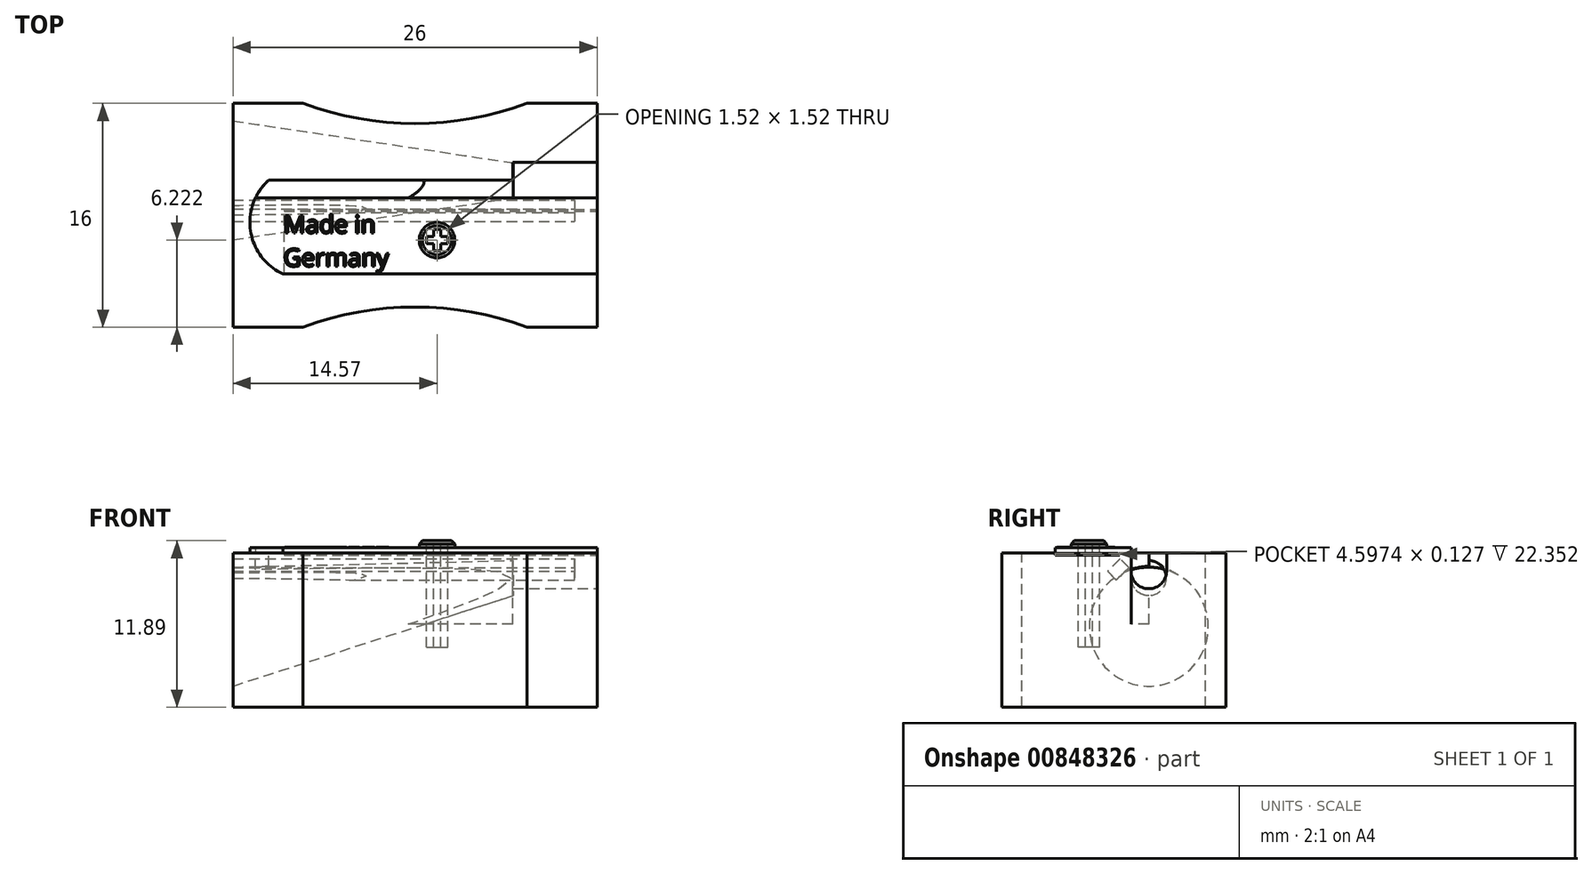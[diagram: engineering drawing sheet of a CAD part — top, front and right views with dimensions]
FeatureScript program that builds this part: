
annotation { "Feature Type Name" : "Feature", "Feature Type Description" : "" }
export const myFeature = defineFeature(function(context is Context, id is Id, definition is map)
    precondition{}
    {
        {
            var Q0;
            Q0=qCreatedBy(makeId("Top.planeOp"),FACE);
            var sketch = newSketch(context, id + "F0", { "sketchPlane" : qUnion([Q0])});
            skLineSegment(sketch, "E0.bottom", {"start": v(-13, 8) * mm, "end": v(13, 8) * mm});
            skLineSegment(sketch, "E0.top", {"start": v(-13, -8) * mm, "end": v(13, -8) * mm});
            skLineSegment(sketch, "E0.left", {"start": v(-13, 8) * mm, "end": v(-13, -8) * mm});
            skLineSegment(sketch, "E0.right", {"start": v(13, 8) * mm, "end": v(13, -8) * mm});
            skSolve(sketch);
        }
        {
            var Q0;
            Q0=makeQuery(id+"F0.imprint","IMPRINT",FACE,{"disambiguationData":[TD([[makeQuery(id+"F0.imprint","IMPRINT",EDGE,{"derivedFrom":sQuery(id+"F0.wireOp",EDGE,"E0.bottom")}),-1.0]])]});
            extrude(context, id + "F1", {"entities" : qUnion([Q0]), "depth" : 11 * mm, "offsetDistance" : 25.4 * mm});
        }
        {
            var Q0;
            Q0=makeQuery(id+"F1.opExtrude","CAP_FACE",FACE,{"disambiguationData":[OSD([sQuery(id+"F0.wireOp",EDGE,"E0.bottom"),sQuery(id+"F0.wireOp",EDGE,"E0.top"),sQuery(id+"F0.wireOp",EDGE,"E0.left"),sQuery(id+"F0.wireOp",EDGE,"E0.right")])],"isStart":false});
            var sketch = newSketch(context, id + "F2", { "sketchPlane" : qUnion([Q0])});
            skArc(sketch, "E1", {"start": v(8, -8) * mm, "mid": v(0, -6.55) * mm, "end": v(-8, -8) * mm});
            skArc(sketch, "E2", {"start": v(-8, 8) * mm, "mid": v(0, 6.55) * mm, "end": v(8, 8) * mm});
            skSolve(sketch);
        }
        {
            var Q0;
            {var subQ0=sQuery(id+"F2.wireOp",EDGE,"E2");Q0=makeQuery(id+"F2.imprint","IMPRINT",FACE,{"disambiguationData":[TD([[makeQuery(id+"F2.imprint","IMPRINT",EDGE,{"derivedFrom":subQ0}),1.0]])]});}
            var Q1;
            {var subQ0=sQuery(id+"F2.wireOp",EDGE,"E1");Q1=makeQuery(id+"F2.imprint","IMPRINT",FACE,{"disambiguationData":[TD([[makeQuery(id+"F2.imprint","IMPRINT",EDGE,{"derivedFrom":subQ0}),1.0]])]});}
            extrude(context, id + "F3", {"entities" : qUnion([Q0, Q1]), "operationType" : NewBodyOperationType.REMOVE, "endBound" : BoundingType.THROUGH_ALL, "oppositeDirection" : true, "depth" : 25.4 * mm, "offsetDistance" : 25.4 * mm});
        }
        {
            var Q0;
            Q0=makeQuery(id+"F1.opExtrude","SWEPT_FACE",FACE,{"disambiguationData":[OSD([sQuery(id+"F0.wireOp",EDGE,"E0.left")])]});
            var sketch = newSketch(context, id + "F4", { "sketchPlane" : qUnion([Q0])});
            skCircle(sketch, "E3", {"center": v(-2.5, 5.75) * mm, "radius": 4.25 * mm});
            skSolve(sketch);
        }
        {
            var Q0;
            Q0=qCreatedBy(makeId("Right.planeOp"),FACE);
            cPlane(context, id + "F5", {"entities" : qUnion([Q0]), "cplaneType" : CPlaneType.OFFSET, "offset" : 7 * mm, "width" : 152.4 * mm, "height" : 152.4 * mm});
        }
        {
            var Q0;
            Q0=qCreatedBy(id+"F5.planeOp",FACE);
            var sketch = newSketch(context, id + "F6", { "sketchPlane" : qUnion([Q0])});
            skCircle(sketch, "E4", {"center": v(2.5, 9.22) * mm, "radius": 1.25 * mm});
            skSolve(sketch);
        }
        {
            var Q0;
            Q0=qCreatedBy(makeId("Front.planeOp"),FACE);
            cPlane(context, id + "F7", {"entities" : qUnion([Q0]), "cplaneType" : CPlaneType.OFFSET, "offset" : 2.5 * mm, "oppositeDirection" : true, "width" : 152.4 * mm, "height" : 152.4 * mm});
        }
        {
            var Q0;
            Q0=qCreatedBy(id+"F7.planeOp",FACE);
            var sketch = newSketch(context, id + "F8", { "sketchPlane" : qUnion([Q0])});
            skLineSegment(sketch, "E5", {"start": v(-13, 5.75) * mm, "end": v(7, 9.22) * mm});
            skSolve(sketch);
        }
        {
            var Q0;
            Q0=sQuery(id+"F8.wireOp",EDGE,"E5");
            var Q1;
            Q1=makeQuery(id+"F4.imprint","IMPRINT",FACE,{"disambiguationData":[TD([[makeQuery(id+"F4.imprint","IMPRINT",EDGE,{"derivedFrom":sQuery(id+"F4.wireOp",EDGE,"E3")}),1.0]])]});
            var Q2;
            Q2 = qSketchRegion(id + "F6", true);
            loft(context, id + "F9", {"operationType" : NewBodyOperationType.REMOVE, "addSections" : true, "spine" : qUnion([Q0]), "sectionCount" : 2, "sheetProfilesArray" : [{ "sheetProfileEntities" : qUnion([Q1]) }, { "sheetProfileEntities" : qUnion([Q2]) }]});
        }
        {
            var Q0;
            Q0=makeQuery(id+"F1.opExtrude","SWEPT_FACE",FACE,{"disambiguationData":[OSD([sQuery(id+"F0.wireOp",EDGE,"E0.right")])]});
            var sketch = newSketch(context, id + "F10", { "sketchPlane" : qUnion([Q0])});
            skArc(sketch, "E6", {"start": v(1.23, 9.73) * mm, "mid": v(2.5, 8.46) * mm, "end": v(3.77, 9.73) * mm});
            skLineSegment(sketch, "E7", {"start": v(1.23, 9.73) * mm, "end": v(1.23, 11) * mm});
            skLineSegment(sketch, "E8", {"start": v(3.77, 9.73) * mm, "end": v(3.77, 11) * mm});
            skSolve(sketch);
        }
        {
            var Q0;
            Q0=makeQuery(id+"F10.imprint","IMPRINT",FACE,{"disambiguationData":[TD([[makeQuery(id+"F10.imprint","IMPRINT",EDGE,{"derivedFrom":sQuery(id+"F10.wireOp",EDGE,"E6")}),1.0]])]});
            extrude(context, id + "F11", {"entities" : qUnion([Q0]), "operationType" : NewBodyOperationType.REMOVE, "oppositeDirection" : true, "depth" : 6.02 * mm, "offsetDistance" : 25.4 * mm});
        }
        {
            var Q0;
            Q0=makeQuery(id+"F1.opExtrude","CAP_FACE",FACE,{"disambiguationData":[OSD([sQuery(id+"F0.wireOp",EDGE,"E0.bottom"),sQuery(id+"F0.wireOp",EDGE,"E0.top"),sQuery(id+"F0.wireOp",EDGE,"E0.left"),sQuery(id+"F0.wireOp",EDGE,"E0.right")])],"isStart":false});
            var sketch = newSketch(context, id + "F12", { "sketchPlane" : qUnion([Q0])});
            skLineSegment(sketch, "E9", {"start": v(6.98, 2.5) * mm, "end": v(-10.46, 2.5) * mm});
            skArc(sketch, "E10", {"start": v(-10.46, 2.5) * mm, "mid": v(-11.74, -1.12) * mm, "end": v(-9.44, -4.2) * mm});
            skLineSegment(sketch, "E11", {"start": v(-9.44, -4.2) * mm, "end": v(13, -4.2) * mm});
            skLineSegment(sketch, "E12", {"start": v(13, 1.23) * mm, "end": v(-11.4, 1.23) * mm});
            skSolve(sketch);
        }
        {
            var Q0;
            {var subQ0=sQuery(id+"F12.wireOp",EDGE,"E9");Q0=makeQuery(id+"F12.imprint","IMPRINT",FACE,{"disambiguationData":[TD([[makeQuery(id+"F12.imprint","IMPRINT",EDGE,{"derivedFrom":subQ0}),1.0]])]});}
            extrude(context, id + "F13", {"entities" : qUnion([Q0]), "operationType" : NewBodyOperationType.REMOVE, "oppositeDirection" : true, "depth" : 5.08 * mm, "offsetDistance" : 25.4 * mm});
        }
        {
            var Q0;
            {var subQ8=sQuery(id+"F12.wireOp",EDGE,"E11");Q0=makeQuery(id+"F12.imprint","IMPRINT",FACE,{"disambiguationData":[TD([[makeQuery(id+"F12.imprint","IMPRINT",EDGE,{"derivedFrom":subQ8}),1.0]])]});}
            extrude(context, id + "F14", {"entities" : qUnion([Q0]), "operationType" : NewBodyOperationType.ADD, "depth" : 0.38 * mm, "offsetDistance" : 25.4 * mm});
        }
        {
            var Q0;
            Q0=makeQuery(id+"F14.opExtrude","CAP_EDGE",EDGE,{"disambiguationData":[OSD([sQuery(id+"F12.wireOp",EDGE,"E12")])],"isStart":false});
            cPlane(context, id + "F15", {"entities" : qUnion([Q0]), "cplaneType" : CPlaneType.LINE_ANGLE, "offset" : 25.4 * mm, "angle" : 45 * degree, "width" : 152.4 * mm, "height" : 152.4 * mm});
        }
        {
            var Q0;
            Q0=qCreatedBy(id+"F15.planeOp",FACE);
            var sketch = newSketch(context, id + "F16", { "sketchPlane" : qUnion([Q0])});
            skLineSegment(sketch, "E13.bottom", {"start": v(-13, 7.81) * mm, "end": v(11.4, 7.81) * mm});
            skLineSegment(sketch, "E13.top", {"start": v(-13, 6.54) * mm, "end": v(11.4, 6.54) * mm});
            skLineSegment(sketch, "E13.left", {"start": v(-13, 7.81) * mm, "end": v(-13, 6.54) * mm});
            skLineSegment(sketch, "E13.right", {"start": v(11.4, 7.81) * mm, "end": v(11.4, 6.54) * mm});
            skPoint(sketch, "E14", {"position": v(-13, 7.18) * mm});
            skPoint(sketch, "E15", {"position": v(11.4, 7.18) * mm});
            skSolve(sketch);
        }
        {
            var Q0;
            Q0=makeQuery(id+"F16.imprint","IMPRINT",FACE,{"disambiguationData":[TD([[makeQuery(id+"F16.imprint","IMPRINT",EDGE,{"derivedFrom":sQuery(id+"F16.wireOp",EDGE,"E13.bottom")}),-1.0]])]});
            extrude(context, id + "F17", {"entities" : qUnion([Q0]), "operationType" : NewBodyOperationType.REMOVE, "oppositeDirection" : true, "depth" : 0.89 * mm, "offsetDistance" : 25.4 * mm});
        }
        {
            var Q0;
            Q0=makeQuery(id+"F14.opExtrude","CAP_FACE",FACE,{"disambiguationData":[OSD([sQuery(id+"F0.wireOp",EDGE,"E0.right"),sQuery(id+"F12.wireOp",EDGE,"E10"),sQuery(id+"F12.wireOp",EDGE,"E11"),sQuery(id+"F12.wireOp",EDGE,"E12")])],"isStart":false});
            var sketch = newSketch(context, id + "F18", { "sketchPlane" : qUnion([Q0])});
            skText(sketch, "E16", { "text": "Made in\nGermany", "fontName": "OpenSans-Regular.ttf"});
            skCircle(sketch, "E17", {"center": v(1.57, -1.78) * mm, "radius": 1.27 * mm});
            const initialGuessF18  = {"E16": [-0.0094, -0.00127, 1, 0, 0.00126]};
            skSetInitialGuess(sketch, initialGuessF18);
            skSolve(sketch);
        }
        {
            var Q0;
            Q0=makeQuery(id+"F18.imprint","IMPRINT",FACE,{"disambiguationData":[TD([[makeQuery(id+"F18.imprint","IMPRINT",EDGE,{"derivedFrom":sQuery(id+"F18.wireOp",EDGE,"E16.sketch_text.stroke-0")}),-1.0]])]});
            var Q1;
            Q1=makeQuery(id+"F18.imprint","IMPRINT",FACE,{"disambiguationData":[TD([[makeQuery(id+"F18.imprint","IMPRINT",EDGE,{"derivedFrom":sQuery(id+"F18.wireOp",EDGE,"E16.sketch_text.stroke-88")}),-1.0]])]});
            var Q2;
            Q2=makeQuery(id+"F18.imprint","IMPRINT",FACE,{"disambiguationData":[TD([[makeQuery(id+"F18.imprint","IMPRINT",EDGE,{"derivedFrom":sQuery(id+"F18.wireOp",EDGE,"E16.sketch_text.stroke-92")}),-1.0]])]});
            var Q3;
            Q3=makeQuery(id+"F18.imprint","IMPRINT",FACE,{"disambiguationData":[TD([[makeQuery(id+"F18.imprint","IMPRINT",EDGE,{"derivedFrom":sQuery(id+"F18.wireOp",EDGE,"E16.sketch_text.stroke-100")}),-1.0]])]});
            var Q4;
            Q4=makeQuery(id+"F18.imprint","IMPRINT",FACE,{"disambiguationData":[TD([[makeQuery(id+"F18.imprint","IMPRINT",EDGE,{"derivedFrom":sQuery(id+"F18.wireOp",EDGE,"E16.sketch_text.stroke-117")}),-1.0]])]});
            var Q5;
            Q5=makeQuery(id+"F18.imprint","IMPRINT",FACE,{"disambiguationData":[TD([[makeQuery(id+"F18.imprint","IMPRINT",EDGE,{"derivedFrom":sQuery(id+"F18.wireOp",EDGE,"E16.sketch_text.stroke-156")}),-1.0]])]});
            var Q6;
            Q6=makeQuery(id+"F18.imprint","IMPRINT",FACE,{"disambiguationData":[TD([[makeQuery(id+"F18.imprint","IMPRINT",EDGE,{"derivedFrom":sQuery(id+"F18.wireOp",EDGE,"E16.sketch_text.stroke-169")}),-1.0]])]});
            var Q7;
            Q7=makeQuery(id+"F18.imprint","IMPRINT",FACE,{"disambiguationData":[TD([[makeQuery(id+"F18.imprint","IMPRINT",EDGE,{"derivedFrom":sQuery(id+"F18.wireOp",EDGE,"E16.sketch_text.stroke-224")}),-1.0]])]});
            var Q8;
            Q8=makeQuery(id+"F18.imprint","IMPRINT",FACE,{"disambiguationData":[TD([[makeQuery(id+"F18.imprint","IMPRINT",EDGE,{"derivedFrom":sQuery(id+"F18.wireOp",EDGE,"E16.sketch_text.stroke-241")}),-1.0]])]});
            var Q9;
            Q9=makeQuery(id+"F18.imprint","IMPRINT",FACE,{"disambiguationData":[TD([[makeQuery(id+"F18.imprint","IMPRINT",EDGE,{"derivedFrom":sQuery(id+"F18.wireOp",EDGE,"E16.sketch_text.stroke-18")}),-1.0]])]});
            var Q10;
            Q10=makeQuery(id+"F18.imprint","IMPRINT",FACE,{"disambiguationData":[TD([[makeQuery(id+"F18.imprint","IMPRINT",EDGE,{"derivedFrom":sQuery(id+"F18.wireOp",EDGE,"E16.sketch_text.stroke-45")}),-1.0]])]});
            var Q11;
            Q11=makeQuery(id+"F18.imprint","IMPRINT",FACE,{"disambiguationData":[TD([[makeQuery(id+"F18.imprint","IMPRINT",EDGE,{"derivedFrom":sQuery(id+"F18.wireOp",EDGE,"E16.sketch_text.stroke-69")}),-1.0]])]});
            var Q12;
            Q12=makeQuery(id+"F18.imprint","IMPRINT",FACE,{"disambiguationData":[TD([[makeQuery(id+"F18.imprint","IMPRINT",EDGE,{"derivedFrom":sQuery(id+"F18.wireOp",EDGE,"E16.sketch_text.stroke-137")}),-1.0]])]});
            var Q13;
            Q13=makeQuery(id+"F18.imprint","IMPRINT",FACE,{"disambiguationData":[TD([[makeQuery(id+"F18.imprint","IMPRINT",EDGE,{"derivedFrom":sQuery(id+"F18.wireOp",EDGE,"E16.sketch_text.stroke-197")}),-1.0]])]});
            extrude(context, id + "F19", {"entities" : qUnion([Q0, Q1, Q2, Q3, Q4, Q5, Q6, Q7, Q8, Q9, Q10, Q11, Q12, Q13]), "operationType" : NewBodyOperationType.ADD, "depth" : 0.05 * mm, "offsetDistance" : 25.4 * mm});
        }
        {
            var Q0;
            Q0=makeQuery(id+"F18.imprint","IMPRINT",FACE,{"disambiguationData":[TD([[makeQuery(id+"F18.imprint","IMPRINT",EDGE,{"derivedFrom":sQuery(id+"F18.wireOp",EDGE,"E17")}),1.0]])]});
            extrude(context, id + "F20", {"entities" : qUnion([Q0]), "operationType" : NewBodyOperationType.ADD, "depth" : 0.5 * mm, "offsetDistance" : 25.4 * mm});
        }
        {
            var Q0;
            Q0=makeQuery(id+"F20.opExtrude","CAP_EDGE",EDGE,{"disambiguationData":[OSD([sQuery(id+"F18.wireOp",EDGE,"E17")])],"isStart":false});
            chamfer(context, id + "F21", {"entities" : qUnion([Q0]), "width" : 0.23 * mm, "tangentPropagation" : true});
        }
        {
            var Q0;
            Q0=makeQuery(id+"F20.opExtrude","CAP_FACE",FACE,{"disambiguationData":[OSD([sQuery(id+"F18.wireOp",EDGE,"E17")])],"isStart":false});
            var sketch = newSketch(context, id + "F22", { "sketchPlane" : qUnion([Q0])});
            skLineSegment(sketch, "E18.bottom", {"start": v(1.32, -1.02) * mm, "end": v(1.82, -1.02) * mm});
            skLineSegment(sketch, "E18.top", {"start": v(1.32, -2.54) * mm, "end": v(1.82, -2.54) * mm});
            skLineSegment(sketch, "E18.left", {"start": v(1.32, -1.02) * mm, "end": v(1.32, -1.52) * mm});
            skLineSegment(sketch, "E18.right", {"start": v(1.82, -1.02) * mm, "end": v(1.82, -1.52) * mm});
            skLineSegment(sketch, "E19.bottom", {"start": v(0.8, -1.52) * mm, "end": v(1.32, -1.52) * mm});
            skLineSegment(sketch, "E19.top", {"start": v(0.8, -2.03) * mm, "end": v(1.32, -2.03) * mm});
            skLineSegment(sketch, "E19.left", {"start": v(0.8, -1.52) * mm, "end": v(0.8, -2.03) * mm});
            skLineSegment(sketch, "E19.right", {"start": v(2.33, -1.52) * mm, "end": v(2.33, -2.03) * mm});
            skLineSegment(sketch, "E20.trimOffspring", {"start": v(1.82, -1.52) * mm, "end": v(2.33, -1.52) * mm});
            skLineSegment(sketch, "E21.trimOffspring", {"start": v(1.32, -2.03) * mm, "end": v(1.32, -2.54) * mm});
            skLineSegment(sketch, "E22.trimOffspring", {"start": v(1.82, -2.03) * mm, "end": v(1.82, -2.54) * mm});
            skLineSegment(sketch, "E23.trimOffspring", {"start": v(1.82, -2.03) * mm, "end": v(2.33, -2.03) * mm});
            skSolve(sketch);
        }
        {
            var Q0;
            Q0=makeQuery(id+"F22.imprint","IMPRINT",FACE,{"disambiguationData":[TD([[makeQuery(id+"F22.imprint","IMPRINT",EDGE,{"derivedFrom":sQuery(id+"F22.wireOp",EDGE,"E18.bottom")}),-1.0]])]});
            extrude(context, id + "F23", {"entities" : qUnion([Q0]), "operationType" : NewBodyOperationType.REMOVE, "oppositeDirection" : true, "depth" : 7.62 * mm, "offsetDistance" : 25.4 * mm});
        }
        {
            var Q0;
            {var subQ0=sQuery(id+"F0.wireOp",EDGE,"E0.right");Q0=makeQuery(id+"F14.boolean.opBoolean","MERGE",FACE,{"derivedFrom":[makeQuery(id+"F1.opExtrude","SWEPT_FACE",FACE,{"disambiguationData":[OSD([subQ0])]}),makeQuery(id+"F14.opExtrude","SWEPT_FACE",FACE,{"disambiguationData":[OSD([subQ0])]})]});}
            var sketch = newSketch(context, id + "F24", { "sketchPlane" : qUnion([Q0])});
            skLineSegment(sketch, "E24.bottom", {"start": v(-4.2, 10.97) * mm, "end": v(0.28, 10.97) * mm});
            skLineSegment(sketch, "E24.top", {"start": v(-4.2, 10.85) * mm, "end": v(0.28, 10.85) * mm});
            skLineSegment(sketch, "E24.left", {"start": v(-4.2, 10.97) * mm, "end": v(-4.2, 10.85) * mm});
            skLineSegment(sketch, "E25", {"start": v(0.4, 10.85) * mm, "end": v(0.28, 10.97) * mm});
            skLineSegment(sketch, "E26", {"start": v(0.28, 10.85) * mm, "end": v(0.4, 10.85) * mm});
            skSolve(sketch);
        }
        {
            var Q0;
            Q0=makeQuery(id+"F24.imprint","IMPRINT",FACE,{"disambiguationData":[TD([[makeQuery(id+"F24.imprint","IMPRINT",EDGE,{"derivedFrom":sQuery(id+"F24.wireOp",EDGE,"E24.bottom")}),-1.0]])]});
            extrude(context, id + "F25", {"entities" : qUnion([Q0]), "operationType" : NewBodyOperationType.REMOVE, "oppositeDirection" : true, "depth" : 22.35 * mm, "offsetDistance" : 25.4 * mm});
        }
    });
